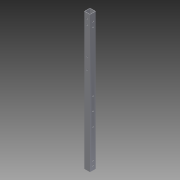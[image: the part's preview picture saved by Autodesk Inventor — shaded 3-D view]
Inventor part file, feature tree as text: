
AUTODESK INVENTOR PART (.ipt)
format: ipt  version: 2014 SP1 (Build 180222100, 222)  size: 119,808 bytes
history: native  units: in
note: dims shown in document units (in); Inventor stores cm internally (conversion verified against a paired STEP export)
features: extrude x4, sketch x4, reference x4
ambient origin geometry x8: Origin, YZ Plane, XZ Plane, XY Plane, X Axis, Y Axis, Z Axis, Center Point
bodies: Solid1 (feature_tree)
feature tree (12):
  extrude  "Extrusion1"  Depth=1.0in
  extrude  "Extrusion6"  Depth=23.5in TaperAngle=0.0deg
  extrude  "Extrusion7"  Depth=1.0in TaperAngle=0.0deg
  extrude  "Extrusion8"  [1 undecoded]
  sketch  "Sketch1"  dims[d0=1.0in d2=1.0in]
  sketch  "Sketch7"  dims[d3=0.0625in d4=23.5in d5=0.0in]
  sketch  "Sketch8"  dims[d18=1.0in d19=0.0in d20=1.0in d21=0.0in]
  sketch  "Sketch9"  dims[d22=1.0in d23=0.0in]
  reference  "Reference15"
  reference  "Reference16"
  reference  "Reference17"
  reference  "Reference18"
note: 1 required parameter value undecoded (feature->parameter linkage not recoverable at this tier; creation-order binding heuristic only, values carry confidence <= 0.55)
